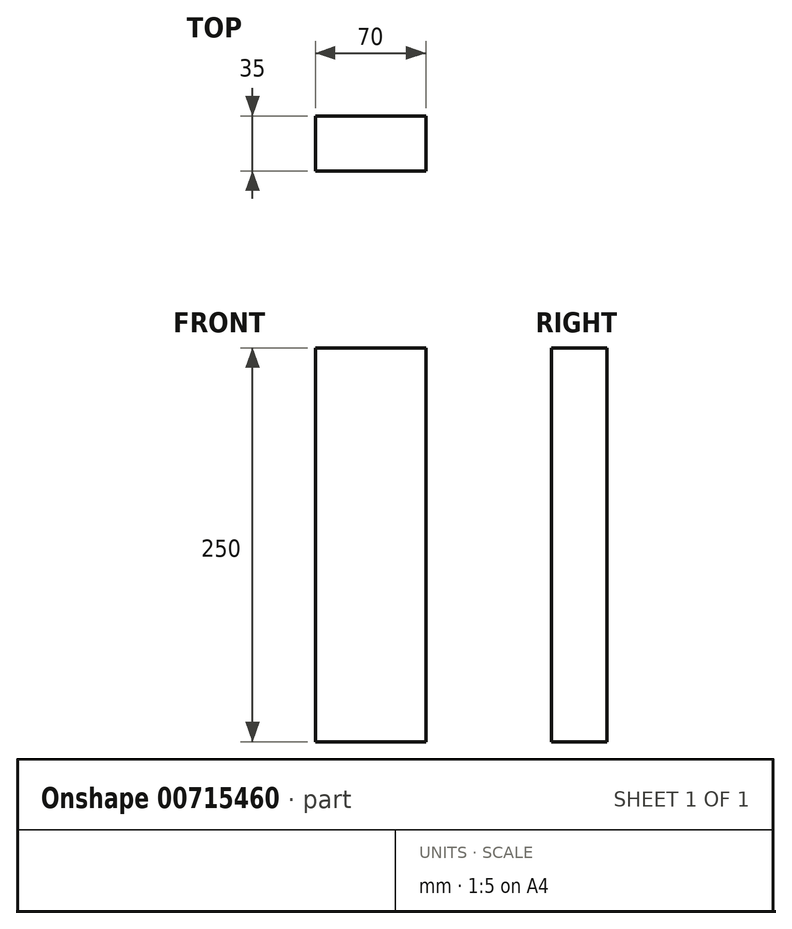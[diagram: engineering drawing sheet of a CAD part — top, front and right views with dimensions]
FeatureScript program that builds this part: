
annotation { "Feature Type Name" : "Feature", "Feature Type Description" : "" }
export const myFeature = defineFeature(function(context is Context, id is Id, definition is map)
    precondition{}
    {
        {
            var Q0;
            Q0=qCreatedBy(makeId("Front.planeOp"),FACE);
            var sketch = newSketch(context, id + "F0", { "sketchPlane" : qUnion([Q0])});
            skLineSegment(sketch, "E0.bottom", {"start": v(-71.4, 0) * mm, "end": v(-1.4, 0) * mm});
            skLineSegment(sketch, "E0.top", {"start": v(-71.4, 250) * mm, "end": v(-1.4, 250) * mm});
            skLineSegment(sketch, "E0.left", {"start": v(-71.4, 0) * mm, "end": v(-71.4, 250) * mm});
            skLineSegment(sketch, "E0.right", {"start": v(-1.4, 0) * mm, "end": v(-1.4, 250) * mm});
            skSolve(sketch);
        }
        {
            var Q0;
            Q0=qSketchRegion(id+"F0",true);
            extrude(context, id + "F1", {"entities" : qUnion([Q0]), "depth" : 35 * mm, "offsetDistance" : 25 * mm});
        }
    });
